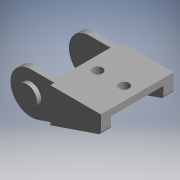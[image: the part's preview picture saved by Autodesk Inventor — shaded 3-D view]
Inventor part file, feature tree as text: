
AUTODESK INVENTOR PART (.ipt)
format: ipt  version: 2017.3 (Build 213256000, 256)  size: 153,088 bytes
history: native  units: mm (DEFAULTED — no unit token found)
features: other x21, extrude x7, sketch x7
ambient origin geometry x8: Origin, YZ Plane, XZ Plane, XY Plane, X Axis, Y Axis, Z Axis, Center Point
bodies: Solid1 (feature_tree)
feature tree (35):
  extrude  "Extrusion1"  Depth=1.85mm TaperAngle=0.0deg
  extrude  "Extrusion2"  Depth=1.85mm TaperAngle=0.0deg
  extrude  "Extrusion3"  Depth=1.4mm TaperAngle=0.0deg
  extrude  "Extrusion4"  TaperAngle=0.0deg  [1 undecoded]
  extrude  "Extrusion5"  [1 undecoded]
  extrude  "Extrusion6"  [1 undecoded]
  extrude  "Extrusion7"  [1 undecoded]
  other  "end_2_XY"
  other  "end_2_YZ"
  other  "end_2_ZX"
  other  "end_2_X"
  other  "end_2_Y"
  other  "end_2_Z"
  other  "end_2_Center"
  other  "end_move_XY"
  other  "end_move_YZ"
  other  "end_move_ZX"
  other  "end_move_X"
  other  "end_move_Y"
  other  "end_move_Z"
  other  "end_move_Center"
  other  "to_dummy_XY"
  other  "to_dummy_YZ"
  other  "to_dummy_ZX"
  other  "to_dummy_X"
  other  "to_dummy_Y"
  other  "to_dummy_Z"
  other  "to_dummy_Center"
  sketch  "Sketch_77"  dims[d0=2.0mm d1=0.0mm d2=1.85mm d3=0.0mm]
  sketch  "Sketch_78"  dims[d4=1.85mm d5=0.0mm d6=1.4mm d7=0.0mm]
  sketch  "Sketch_79"  dims[d8=2.8mm d9=0.0mm d10=1.4mm d11=0.0mm]
  sketch  "Sketch_80"  dims[d12=2.8mm d13=0.0mm d14=0.0mm]
  sketch  "Sketch_81"
  sketch  "Sketch_82"
  sketch  "Sketch_83"
note: 4 required parameter values undecoded (feature->parameter linkage not recoverable at this tier; creation-order binding heuristic only, values carry confidence <= 0.55)
